# Revit family: streetlight_sl_31_maxi___st1_0a_5xh4d3bn08ta_7b71
name_source: partatom
category: Lighting Fixtures
units: mm (PartAtom-declared; Revit-internal decimal feet)

## family parameters
Cut with Voids When Loaded = No
Host = Face
Light Source = No
Part Type = Normal
Room Calculation Point = No
Round Connector Dimension = Use Diameter
Shared = No

## types (1)
- --- (1 x LED, 32370 lm, 217.7 W, 3000K)
    Apparent Load = 218 VA
    CIE Flux Codes = 40 73 97 100 100
    Color Rendering = 70
    Color Temperature = 3000K
    Default Elevation = 1800 mm
    Description = Streetlight SL 31 maxi, mast luminaire, primary light control with lens, of PMMA, primary optical cover: cover, of toughened safety glass, transparent, light distribution: ST1.0a, light emission: direct distribution, primary light characteristic: asymmetric, installation type: post-top, side-entry, LED, High Power LED, rated luminous flux: 32.370lm, luminous efficacy: 149lm/W, light colour: 730, colour temperature: 3000K, control: overheat protection, intelligent temperature release in ECG and LED module, constant luminous flux control, time-dependent luminous flux control, flexible luminous flux parameterisation, presetting dimming linear, with cable H07RN-F 3x 1.5mm², mains connection: 220..240V, AC, 50/60Hz, connection cable pre-assembled, cable length: 14,5m, start of lifetime: 218W, end of service life: 235W, reduction: 100W, luminaire housing, of diecast aluminium, powder-coated, Siteco® metallic grey (DB 702S), corrosivity category C5 high according to DIN EN ISO 12944, no sealing on luminaire upper side, inclination: -15°..+20° (post-top) | -20°..+20° (side-entry), adjustable in 5° steps, mast flange (76/60mm) included as standard, multi-level sealing system, sealing non-destructively replaceable, protection rating (complete): IP66, insulation class (complete): insulation class I (protective earthing), certification: CE, ENEC, ENEC+, VDE, UKCA, impact resistance: IK09, permissible operating ambient temperature for outdoor applications: -40..+50°C, standard-compliant lighting for roads and squares, packaging unit: 1 piece

Light Distribution: ST1.0a
    Height = 79 mm
    Lamp = 1 x LED
    Lamp Light Flux = 32370 lm
    Lamp Power = 217.7 W
    Lamp count = 1
    Length = 657 mm
    Luminous efficacy = 149 lm/W
    Manufacturer = Siteco
    ModVariant = No
    Model = 5XH4D3BN08TA
    Number of Poles = 1
    OnlyDefault = Yes
    Power Factor = 1
    Product Name = Streetlight SL 31 maxi | ST1.0a
    Product group = mast luminaire | pylon top
    ProductGroupID = 6100
    Protection Class = Protection class I
    Protection Degree = IP 66
    RLX_Detail_Level = 1
    RLX_Emergency_Light_Flux = 0 lm
    RLX_Emergency_Type = 0
    RLX_Emergency_Type_DB = No
    RlxData = <blob elided: 47565 chars, md5=6fea0a45>
    Socket = socket
    Standby Power = 0 W
    System Light Flux = 32370 lm
    System Power = 218 W
    Type Comments = factory setting: luminous flux: 100 % | dim-lin: 254 | 765 mA
    Type Image = l_1300293.jpg
    URL = http://relux.com
    VarID = @adj_000839
    Voltage = 0 V
    Weight = 0.00 kg
    Width = 362 mm

## geometry (parser evidence)
native form markers: Sweep x12
no freeform markers — native parametric forms only
